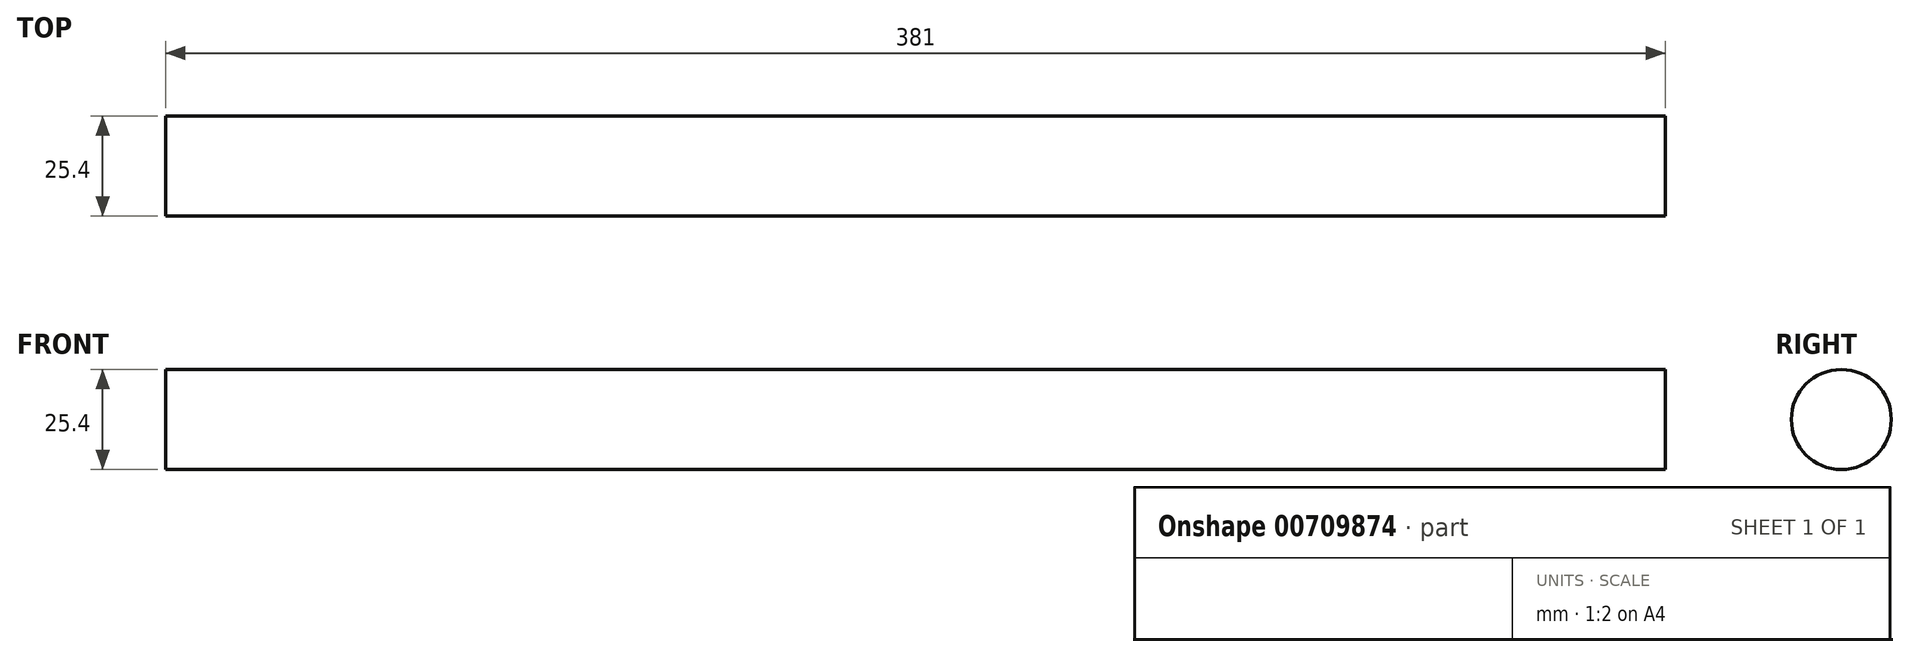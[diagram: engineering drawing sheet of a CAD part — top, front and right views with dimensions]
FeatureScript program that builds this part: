
annotation { "Feature Type Name" : "Feature", "Feature Type Description" : "" }
export const myFeature = defineFeature(function(context is Context, id is Id, definition is map)
    precondition{}
    {
        {
            var Q0;
            Q0=qCreatedBy(makeId("Right.planeOp"),FACE);
            var sketch = newSketch(context, id + "F0", { "sketchPlane" : qUnion([Q0])});
            skCircle(sketch, "E0", {"center": v(0, 0) * mm, "radius": 12.7 * mm});
            skSolve(sketch);
        }
        {
            var Q0;
            Q0 = qSketchRegion(id + "F0", true);
            extrude(context, id + "F1", {"entities" : qUnion([Q0]), "endBound" : BoundingType.SYMMETRIC, "depth" : 381 * mm, "offsetDistance" : 25.4 * mm});
        }
    });
